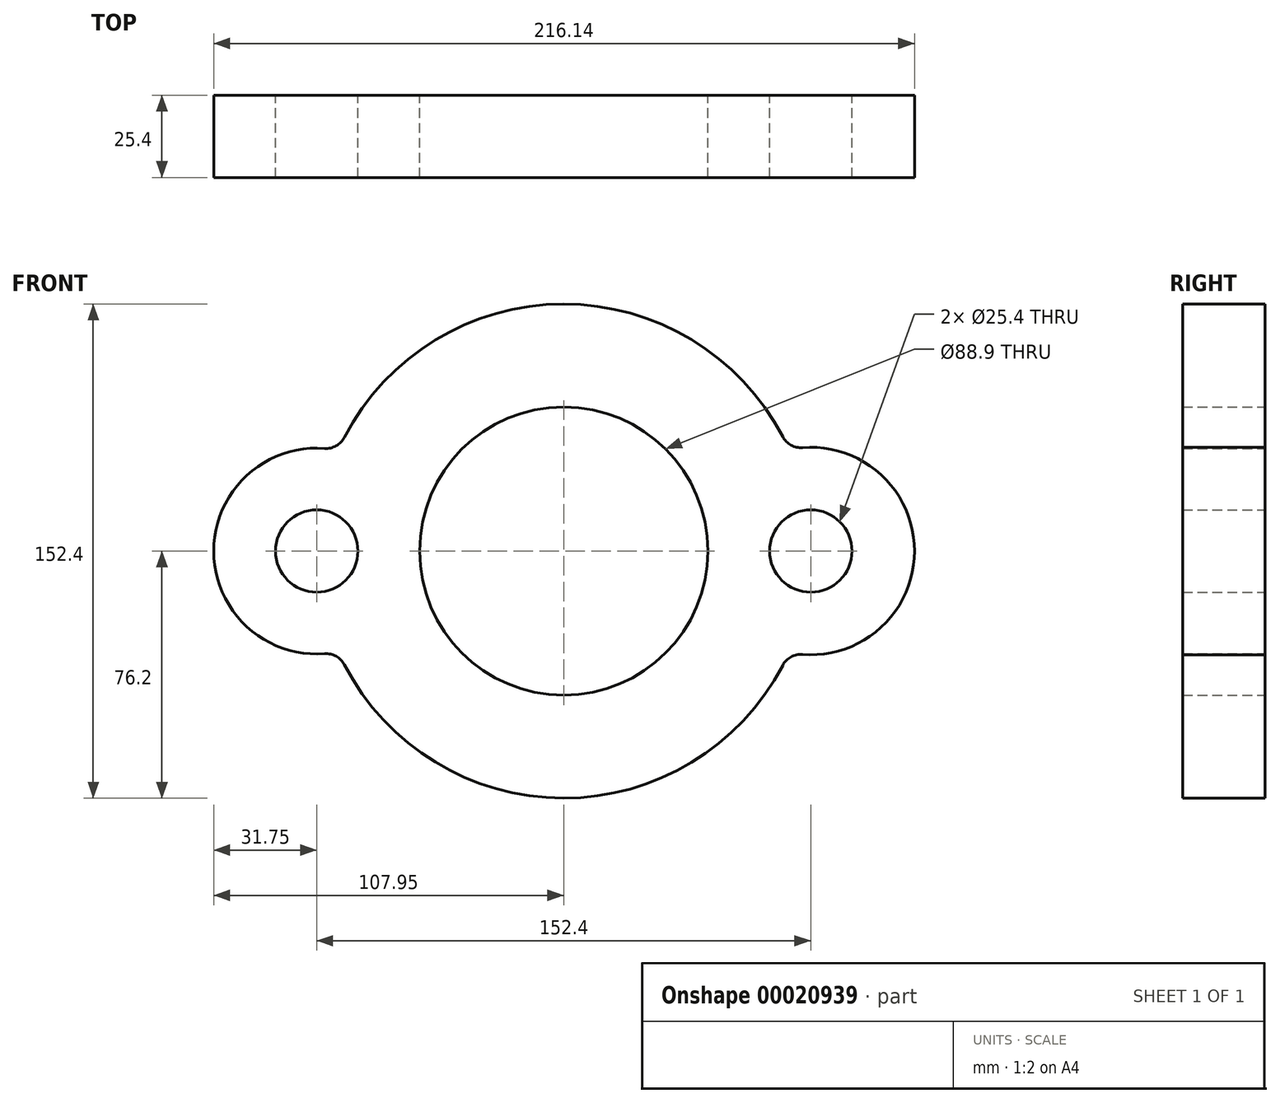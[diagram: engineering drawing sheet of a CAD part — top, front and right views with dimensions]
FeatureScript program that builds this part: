
annotation { "Feature Type Name" : "Feature", "Feature Type Description" : "" }
export const myFeature = defineFeature(function(context is Context, id is Id, definition is map)
    precondition{}
    {
        {
            var Q0;
            Q0=qCreatedBy(makeId("Front.planeOp"),FACE);
            var sketch = newSketch(context, id + "F0", { "sketchPlane" : qUnion([Q0])});
            skCircle(sketch, "E0", {"center": v(0, 0) * mm, "radius": 44.45 * mm});
            skArc(sketch, "E1", {"start": v(67.54, 35.28) * mm, "mid": v(-0.12, 76.2) * mm, "end": v(-67.65, 35.07) * mm});
            skLineSegment(sketch, "E2", {"start": v(44.2, 0) * mm, "end": v(44.45, 0) * mm});
            skArc(sketch, "E3", {"start": v(-73.77, 31.66) * mm, "mid": v(-107.95, 0) * mm, "end": v(-73.77, -31.66) * mm});
            skArc(sketch, "E4", {"start": v(73.67, -31.9) * mm, "mid": v(108.2, 0) * mm, "end": v(73.67, 31.9) * mm});
            skCircle(sketch, "E5", {"center": v(76.2, 0) * mm, "radius": 12.7 * mm});
            skCircle(sketch, "E6", {"center": v(-76.2, 0) * mm, "radius": 12.7 * mm});
            skArc(sketch, "E7.trimOffspring", {"start": v(75.14, -12.66) * mm, "mid": v(76.2, 0) * mm, "end": v(75.14, 12.66) * mm});
            skArc(sketch, "E8.trimOffspring", {"start": v(-67.65, -35.07) * mm, "mid": v(-0.12, -76.2) * mm, "end": v(67.54, -35.28) * mm});
            skArc(sketch, "E9.trimOffspring", {"start": v(-75.14, 12.66) * mm, "mid": v(-76.2, 0) * mm, "end": v(-75.14, -12.66) * mm});
            skPoint(sketch, "E10.visualSharp", {"position": v(-69.59, 31.05) * mm});
            skArc(sketch, "E10.filletArc", {"start": v(-73.77, 31.66) * mm, "mid": v(-70.2, 32.44) * mm, "end": v(-67.65, 35.07) * mm});
            skPoint(sketch, "E11.visualSharp", {"position": v(-69.59, -31.05) * mm});
            skArc(sketch, "E11.filletArc", {"start": v(-67.65, -35.07) * mm, "mid": v(-70.2, -32.44) * mm, "end": v(-73.77, -31.66) * mm});
            skPoint(sketch, "E12.visualSharp", {"position": v(69.48, -31.28) * mm});
            skArc(sketch, "E12.filletArc", {"start": v(73.67, -31.9) * mm, "mid": v(70.1, -32.66) * mm, "end": v(67.54, -35.28) * mm});
            skPoint(sketch, "E13.visualSharp", {"position": v(69.48, 31.28) * mm});
            skArc(sketch, "E13.filletArc", {"start": v(67.54, 35.28) * mm, "mid": v(70.1, 32.66) * mm, "end": v(73.67, 31.9) * mm});
            skPoint(sketch, "E14.trimOffspring.end.orphan", {"position": v(-105.48, 0) * mm});
            skSolve(sketch);
        }
        {
            var Q0;
            Q0=makeQuery(id+"F0.imprint","IMPRINT",FACE,{"disambiguationData":[TD([[makeQuery(id+"F0.imprint","IMPRINT",EDGE,{"derivedFrom":sQuery(id+"F0.wireOp",EDGE,"E0")}),-1.0]])]});
            extrude(context, id + "F1", {"entities" : qUnion([Q0]), "depth" : 25.4 * mm});
        }
    });
